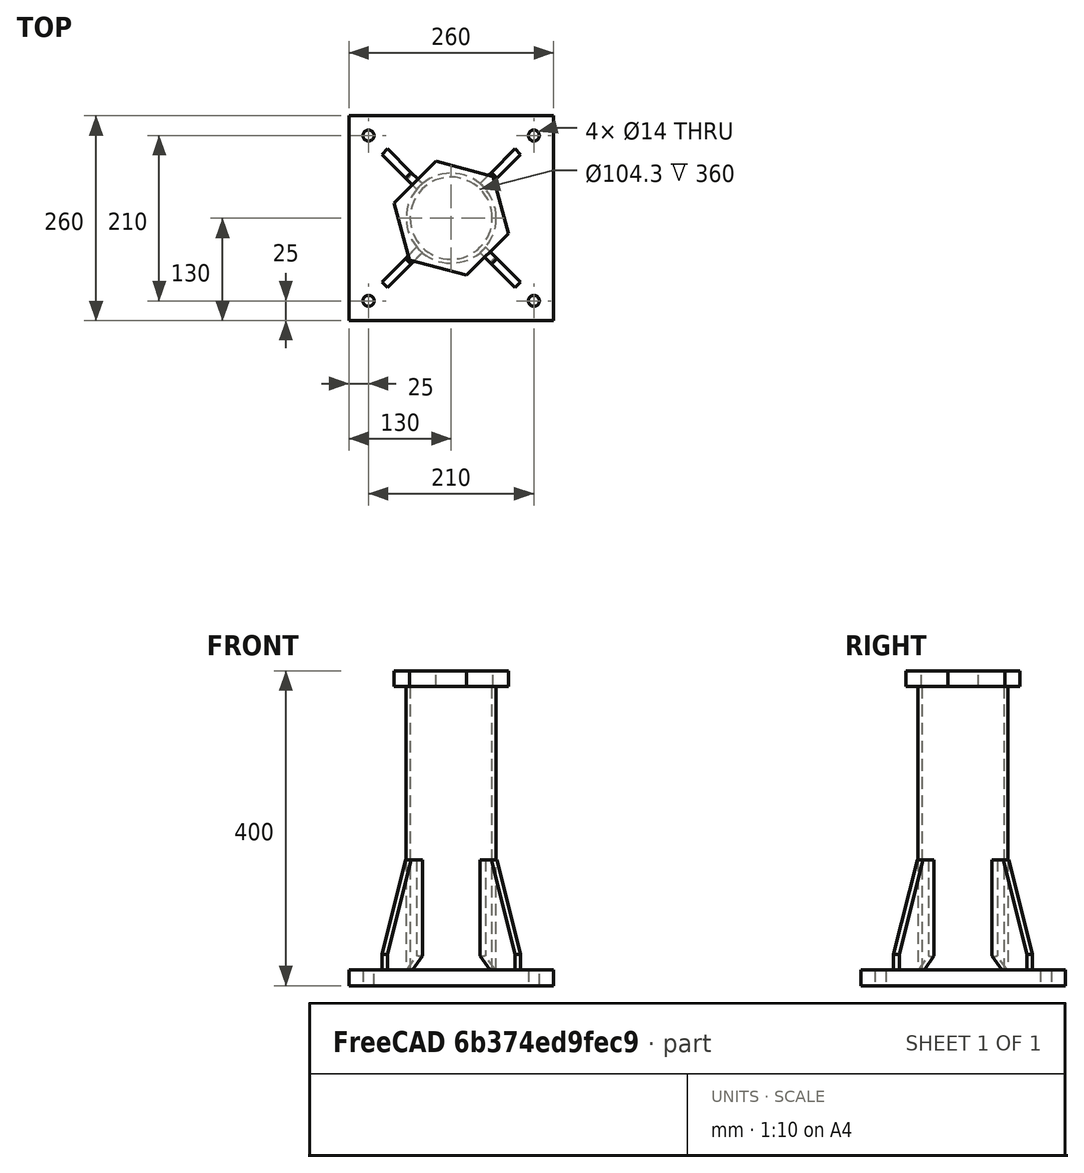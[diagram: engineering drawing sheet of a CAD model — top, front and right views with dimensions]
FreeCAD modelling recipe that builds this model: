
FCSTD DOCUMENT  (FreeCAD 0.21R33694 (Git))
Label: Wyk_Rohrstoss_linear
License: All rights reserved
LicenseURL: http://en.wikipedia.org/wiki/All_rights_reserved
objects: Sketcher::SketchObject×4, Part::Extrusion×4, Fem::ConstraintFixed×4, Fem::ConstraintForce×3, Part::FeaturePython×1, Part::MultiFuse×1, Fem::FemMeshObjectPython×1, Fem::FemSolverObjectPython×1, App::MaterialObjectPython×1, Fem::FemAnalysis×1
note: 10 computed .brp shape members not serialized (recipe doc carries the construction recipe); baked Part::Feature solids carry a one-line shape summary decoded from their .brp

FEATURE [Sketcher::SketchObject] Sketch
  FullyConstrained = true
  sketch-geometry (12):
    g0: LineSegment StartX=-130 StartY=130 StartZ=0 EndX=130 EndY=130 EndZ=0
    g1: LineSegment StartX=130 StartY=130 StartZ=0 EndX=130 EndY=-130 EndZ=0
    g2: LineSegment StartX=130 StartY=-130 StartZ=0 EndX=-130 EndY=-130 EndZ=0
    g3: LineSegment StartX=-130 StartY=-130 StartZ=0 EndX=-130 EndY=130 EndZ=0
    g4: LineSegment StartX=-105 StartY=105 StartZ=0 EndX=105 EndY=105 EndZ=0
    g5: LineSegment StartX=105 StartY=105 StartZ=0 EndX=105 EndY=-105 EndZ=0
    g6: LineSegment StartX=105 StartY=-105 StartZ=0 EndX=-105 EndY=-105 EndZ=0
    g7: LineSegment StartX=-105 StartY=-105 StartZ=0 EndX=-105 EndY=105 EndZ=0
    g8: Circle CenterX=-105 CenterY=105 CenterZ=0 NormalX=0 NormalY=0 NormalZ=1 AngleXU=0 Radius=7
    g9: Circle CenterX=105 CenterY=105 CenterZ=0 NormalX=0 NormalY=0 NormalZ=1 AngleXU=0 Radius=7
    g10: Circle CenterX=-105 CenterY=-105 CenterZ=0 NormalX=0 NormalY=0 NormalZ=1 AngleXU=0 Radius=7
    g11: Circle CenterX=105 CenterY=-105 CenterZ=0 NormalX=0 NormalY=0 NormalZ=1 AngleXU=0 Radius=7
  constraints (28):
    c: Coincident(g0,g1)
    c: Coincident(g1,g2)
    c: Coincident(g2,g3)
    c: Coincident(g3,g0)
    c: Horizontal(g0)
    c: Vertical(g1)
    c: Symmetric(g2,g1,g-2)
    c: Symmetric(g2,g0,g-1)
    c: Equal(g2,g3)
    c: DistanceX(g2,g2) = 260
    c: Coincident(g4,g5)
    c: Coincident(g5,g6)
    c: Coincident(g6,g7)
    c: Coincident(g7,g4)
    c: Horizontal(g4)
    c: Vertical(g7)
    c: Symmetric(g5,g4,g-1)
    c: Symmetric(g6,g5,g-2)
    c: Equal(g6,g5)
    c: DistanceX(g6,g6) = 210
    c: Coincident(g8,g4)
    c: Coincident(g9,g4)
    c: Coincident(g10,g6)
    c: Coincident(g11,g5)
    c: Equal(g8,g9)
    c: Equal(g8,g11)
    c: Equal(g8,g10)
    c: Diameter(g8) = 14
FEATURE [Part::Extrusion] Extrude  label="platte"
  Base = -> Sketch
  Dir = (0,0,1)
  DirMode = 2
  FaceMakerClass = Part::FaceMakerBullseye
  LengthFwd = 20
  LengthRev = 0
  Solid = true
  Symmetric = false
FEATURE [Sketcher::SketchObject] Sketch001
  FullyConstrained = true
  MapMode = 5
  Placement = pos=(0,0,20) rot=(0,0,1;0rad)
  Support = -> [Extrude]
  sketch-geometry (3):
    g0: Circle CenterX=0 CenterY=0 CenterZ=0 NormalX=0 NormalY=0 NormalZ=1 AngleXU=0 Radius=57.15
    g1: Circle CenterX=0 CenterY=0 CenterZ=0 NormalX=0 NormalY=0 NormalZ=1 AngleXU=0 Radius=52.15
    g2: LineSegment StartX=52.15 StartY=0 StartZ=0 EndX=57.15 EndY=0 EndZ=0
  constraints (8):
    c: Coincident(g0,g-1)
    c: Coincident(g1,g0)
    c: Diameter(g0) = 114.3
    c: PointOnObject(g2,g1)
    c: PointOnObject(g2,g0)
    c: PointOnObject(g2,g-1)
    c: Horizontal(g2)
    c: DistanceX(g2,g2) = 5
FEATURE [Part::Extrusion] Extrude001  label="R114x5"
  Base = -> Sketch001
  Dir = (0,0,1)
  DirMode = 2
  FaceMakerClass = Part::FaceMakerBullseye
  LengthFwd = 360
  LengthRev = 0
  Solid = true
  Symmetric = false
FEATURE [Sketcher::SketchObject] Sketch002
  ExternalGeometry = -> [Extrude]
  FullyConstrained = true
  Placement = pos=(0,0,0) rot=(1,0,0;1.5708rad)
  sketch-geometry (6):
    g0: LineSegment StartX=54.65 StartY=160 StartZ=0 EndX=77.15 EndY=160 EndZ=0
    g1: LineSegment StartX=77.15 StartY=160 StartZ=0 EndX=119.65 EndY=40 EndZ=0
    g2: LineSegment StartX=119.65 StartY=40 StartZ=0 EndX=119.65 EndY=20 EndZ=0
    g3: LineSegment StartX=119.65 StartY=20 StartZ=0 EndX=74.65 EndY=20 EndZ=0
    g4: LineSegment StartX=74.65 StartY=20 StartZ=0 EndX=54.65 EndY=40 EndZ=0
    g5: LineSegment StartX=54.65 StartY=40 StartZ=0 EndX=54.65 EndY=160 EndZ=0
  constraints (18):
    c: Horizontal(g0)
    c: Coincident(g0,g1)
    c: Coincident(g1,g2)
    c: Vertical(g2)
    c: Coincident(g2,g3)
    c: Coincident(g3,g4)
    c: Coincident(g4,g5)
    c: Coincident(g5,g0)
    c: Vertical(g5)
    c: Horizontal(g3)
    c: Horizontal(g2,g-3)
    c: DistanceY(g3,g4) = 20
    c: DistanceX(g4,g3) = 20
    c: DistanceX(g4,g2) = 65
    c: DistanceY(g2,g2) = 20
    c: DistanceX(g-1,g4) = 54.65
    c: DistanceX(g0,g0) = 22.5
    c: DistanceY(g2,g0) = 140
FEATURE [Part::Extrusion] Extrude002
  Base = -> Sketch002
  Dir = (0,-1,2e-16)
  DirMode = 2
  FaceMakerClass = Part::FaceMakerBullseye
  LengthFwd = 10
  LengthRev = 0
  Solid = true
  Symmetric = true
FEATURE [Part::FeaturePython] Array  label="steifen"  # Draft array (typed FeaturePython)
  Angle = 360
  ArrayType = 1
  Axis = (0,0,1)
  Base = -> Extrude002
  Center = (0,0,0)
  Count = 4
  Fuse = false
  IntervalAxis = (0,0,0)
  IntervalX = (50,0,0)
  IntervalY = (0,50,0)
  IntervalZ = (0,0,50)
  NumberCircles = 3
  NumberPolar = 4
  NumberX = 2
  NumberY = 2
  NumberZ = 1
  Placement = pos=(0,0,0) rot=(0,0,1;0.785398rad)
  RadialDistance = 50
  Symmetry = 1
  TangentialDistance = 25
FEATURE [Sketcher::SketchObject] Sketch003
  FullyConstrained = true
  MapMode = 5
  Placement = pos=(0,0,380) rot=(0,0,1;0rad)
  Support = -> [Extrude001]
  sketch-geometry (8):
    g0: LineSegment StartX=72.4981 StartY=-19.4258 StartZ=0 EndX=53.0723 EndY=53.0723 EndZ=0
    g1: LineSegment StartX=53.0723 StartY=53.0723 StartZ=0 EndX=-19.4258 EndY=72.4981 EndZ=0
    g2: LineSegment StartX=-19.4258 StartY=72.4981 StartZ=0 EndX=-72.4981 EndY=19.4258 EndZ=0
    g3: LineSegment StartX=-72.4981 StartY=19.4258 StartZ=0 EndX=-53.0723 EndY=-53.0723 EndZ=0
    g4: LineSegment StartX=-53.0723 StartY=-53.0723 StartZ=0 EndX=19.4258 EndY=-72.4981 EndZ=0
    g5: LineSegment StartX=19.4258 StartY=-72.4981 StartZ=0 EndX=72.4981 EndY=-19.4258 EndZ=0
    g6: Circle CenterX=0 CenterY=0 CenterZ=0 NormalX=0 NormalY=0 NormalZ=1 AngleXU=0 Radius=75.0555
    g7: LineSegment StartX=0 StartY=0 StartZ=0 EndX=45.9619 EndY=-45.9619 EndZ=0
  constraints (18):
    c: Coincident(g0,g1)
    c: Coincident(g1,g2)
    c: Coincident(g2,g3)
    c: Coincident(g3,g4)
    c: Coincident(g4,g5)
    c: Coincident(g5,g0)
    c: Equal(g0, g1-g5) x5
    c: PointOnObject(g0,g6)
    c: PointOnObject(g1,g6)
    c: PointOnObject(g2,g6)
    c: PointOnObject(g3,g6)
    c: PointOnObject(g4,g6)
    c: Coincident(g6,g-1)
    c: Coincident(g7,g6)
    c: PointOnObject(g7,g5)
    c: Symmetric(g4,g0,g7)
    c: Angle(g7,g-1) = 0.785398
    c: Distance(g1,g0) = 130
FEATURE [Part::Extrusion] Extrude003  label="lastplatte"
  Base = -> Sketch003
  Dir = (0,0,1)
  DirMode = 2
  FaceMakerClass = Part::FaceMakerBullseye
  LengthFwd = 20
  LengthRev = 0
  Solid = true
  Symmetric = false
FEATURE [Part::MultiFuse] Fusion
  Refine = true
  Shapes = -> [Extrude,Extrude001,Array,Extrude003]
FEATURE [Fem::FemMeshObjectPython] FEMMeshGmsh  # FEM object (typed FeaturePython)
  Algorithm2D = 0
  Algorithm3D = 0
  CharacteristicLengthMax = 8
  CharacteristicLengthMin = 0
  CoherenceMesh = true
  ElementDimension = 3
  ElementOrder = 1
  GeometryTolerance = 1e-06
  GroupsOfNodes = false
  HighOrderOptimize = 0
  MeshSizeFromCurvature = 16
  OptimizeNetgen = false
  OptimizeStd = true
  Part = -> Fusion
  RecombinationAlgorithm = 0
  Recombine3DAll = false
  RecombineAll = false
  SecondOrderLinear = false
FEATURE [Fem::FemSolverObjectPython] SolverCcxTools  # FEM object (typed FeaturePython)
  AnalysisType = 0
  BeamShellResultOutput3D = true
  BucklingFactors = 1
  EigenmodeHighLimit = 1000000
  EigenmodeLowLimit = 0
  EigenmodesCount = 10
  GeometricalNonlinearity = 0
  IterationsControlParameterCutb = 0.25,0.5,0.75,0.85,,,1.5,
  IterationsControlParameterIter = 4,8,9,200,10,400,,200,,
  IterationsControlParameterTimeUse = false
  IterationsThermoMechMaximum = 2000
  IterationsUserDefinedIncrementations = false
  IterationsUserDefinedTimeStepLength = false
  MaterialNonlinearity = 0
  MatrixSolverType = 1
  SplitInputWriter = true
  ThermoMechSteadyState = true
  TimeEnd = 1
  TimeInitialStep = 0.01
FEATURE [App::MaterialObjectPython] MaterialSolid  label="S235"  # material (typed FeaturePython)
  Category = 0
  Material = AuthorAndLicense=(c) 2013 Juergen Riegel (CC-BY 3.0),CardName=CalculiX-Steel,Density=7900 kg/m^3,+8 more (map truncated)
FEATURE [Fem::ConstraintFixed] ConstraintFixed
  NormalDirection = (1,-1e-16,0)
  Normals = (12) [(-1,0,0),(0.5,-0.866025,0),(0.5,0.866025,0),(-1,2.44929e-16,0),(-1,0,0),(0.5,-0.866025,0),(0.5,0.866025,0),(-1,2.44929e-16,0),(-1,0,0),+3 more]
  Points = (12) [(-98,105,20),(-108.5,111.062,20),(-108.5,98.9378,20),(-98,105,20),(-98,105,10),(-108.5,111.062,10),(-108.5,98.9378,10),(-98,105,10),(-98,105,0),+3 more]
  References = -> [Fusion]
  Scale = 4
FEATURE [Fem::ConstraintFixed] ConstraintFixed001
  NormalDirection = (1,-1e-16,0)
  Normals = (12) [(-1,0,0),(0.5,-0.866025,0),(0.5,0.866025,0),(-1,2.44929e-16,0),(-1,0,0),(0.5,-0.866025,0),(0.5,0.866025,0),(-1,2.44929e-16,0),(-1,0,0),+3 more]
  Points = (12) [(112,-105,20),(101.5,-98.9378,20),(101.5,-111.062,20),(112,-105,20),(112,-105,10),(101.5,-98.9378,10),(101.5,-111.062,10),(112,-105,10),(112,-105,0),+3 more]
  References = -> [Fusion]
  Scale = 4
FEATURE [Fem::ConstraintFixed] ConstraintFixed002
  NormalDirection = (1,-1e-16,0)
  Normals = (12) [(-1,0,0),(0.5,-0.866025,0),(0.5,0.866025,0),(-1,2.44929e-16,0),(-1,0,0),(0.5,-0.866025,0),(0.5,0.866025,0),(-1,2.44929e-16,0),(-1,0,0),+3 more]
  Points = (12) [(-98,-105,20),(-108.5,-98.9378,20),(-108.5,-111.062,20),(-98,-105,20),(-98,-105,10),(-108.5,-98.9378,10),(-108.5,-111.062,10),(-98,-105,10),+4 more]
  References = -> [Fusion]
  Scale = 4
FEATURE [Fem::ConstraintFixed] ConstraintFixed003
  NormalDirection = (1,-1e-16,0)
  Normals = (12) [(-1,0,0),(0.5,-0.866025,0),(0.5,0.866025,0),(-1,2.44929e-16,0),(-1,0,0),(0.5,-0.866025,0),(0.5,0.866025,0),(-1,2.44929e-16,0),(-1,0,0),+3 more]
  Points = (12) [(112,105,20),(101.5,111.062,20),(101.5,98.9378,20),(112,105,20),(112,105,10),(101.5,111.062,10),(101.5,98.9378,10),(112,105,10),(112,105,0),+3 more]
  References = -> [Fusion]
  Scale = 4
FEATURE [Fem::ConstraintForce] ConstraintForce
  Direction = -> Fusion [Edge113]
  DirectionVector = (0,0,-1)
  Force = 65330
  NormalDirection = (0.707107,-0.707107,0)
  Points = (12) [(19.4258,-72.4981,400),(37.1166,-54.8073,400),(54.8073,-37.1166,400),(72.4981,-19.4258,400),(19.4258,-72.4981,390),(37.1166,-54.8073,390),+6 more]
  References = -> [Fusion]
  Reversed = true
  Scale = 6
FEATURE [Fem::ConstraintForce] ConstraintForce001
  Direction = -> Fusion [Edge113]
  DirectionVector = (0,0,1)
  Force = 65330
  NormalDirection = (-0.707107,0.707107,0)
  Points = (12) [(-19.4258,72.4981,400),(-37.1166,54.8073,400),(-54.8073,37.1166,400),(-72.4981,19.4258,400),(-19.4258,72.4981,390),(-37.1166,54.8073,390),+6 more]
  References = -> [Fusion]
  Scale = 6
FEATURE [Fem::ConstraintForce] ConstraintForce002
  Direction = -> Fusion [Edge64]
  DirectionVector = (0.707107,-0.707107,0)
  Force = 4410
  NormalDirection = (0,0,1)
  Points = (4) [(24.166,-24.166,400),(24.166,24.166,400),(-24.166,-24.166,400),(-24.166,24.166,400)]
  References = -> [Fusion]
  Scale = 12
FEATURE [Fem::FemAnalysis] Analysis
  Group = -> [SolverCcxTools,MaterialSolid,ConstraintFixed,ConstraintFixed001,ConstraintFixed002,ConstraintFixed003,ConstraintForce,ConstraintForce001,FEMMeshGmsh,ConstraintForce002]
